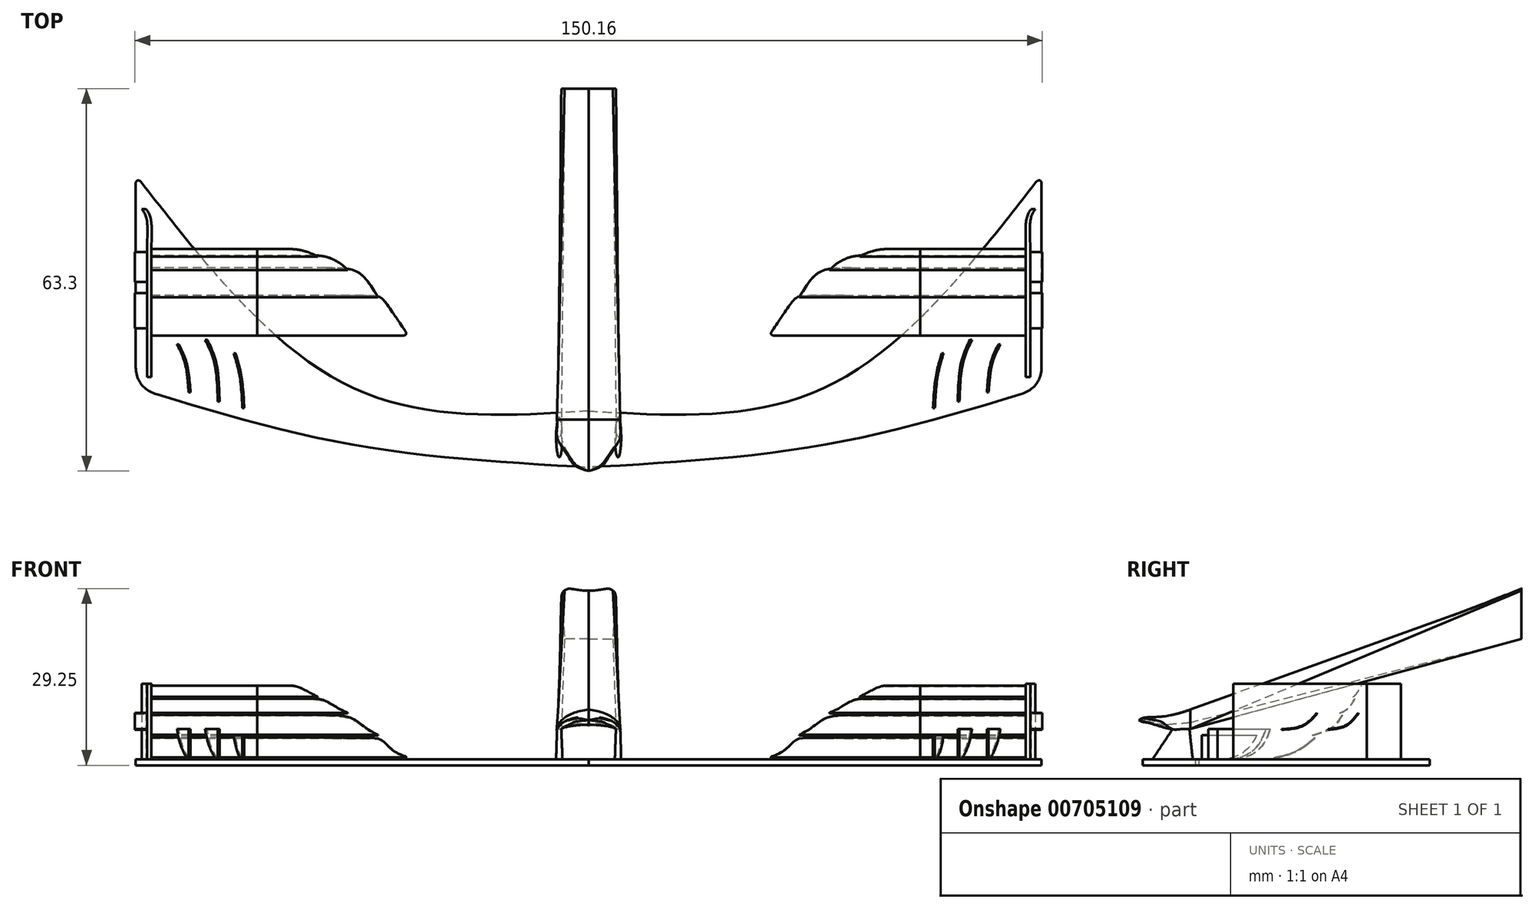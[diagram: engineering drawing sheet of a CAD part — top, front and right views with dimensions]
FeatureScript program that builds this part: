
annotation { "Feature Type Name" : "Feature", "Feature Type Description" : "" }
export const myFeature = defineFeature(function(context is Context, id is Id, definition is map)
    precondition{}
    {
        {
            var Q0;
            Q0=qCreatedBy(makeId("Top.planeOp"),FACE);
            var sketch = newSketch(context, id + "F0", { "sketchPlane" : qUnion([Q0])});
            skLineSegment(sketch, "E0", {"start": v(74.97, -59.54) * mm, "end": v(74.97, -24.29) * mm});
            skFitSpline(sketch, "E1", {"points": [v(74.97, -59.54) * mm, v(39.02, -68.96) * mm, v(0, -72.68) * mm], "startDerivative": vector(-71.84, -22) * mm, "endDerivative": vector(-78.07, -4.37) * mm});
            skFitSpline(sketch, "E2", {"points": [v(0, -63.37) * mm, v(39.02, -59.54) * mm, v(74.97, -24.29) * mm], "startDerivative": vector(86.9, -5.45) * mm, "endDerivative": vector(63.53, 81.8) * mm});
            skFitSpline(sketch, "E3.MirrorCS", {"points": [v(0, -63.37) * mm, v(-39.02, -59.54) * mm, v(-74.97, -24.29) * mm], "startDerivative": vector(-86.9, -5.45) * mm, "endDerivative": vector(-63.53, 81.8) * mm});
            skLineSegment(sketch, "E4.MirrorCS", {"start": v(-74.97, -59.54) * mm, "end": v(-74.97, -24.29) * mm});
            skFitSpline(sketch, "E5.MirrorCS", {"points": [v(-74.97, -59.54) * mm, v(-39.02, -68.96) * mm, v(0, -72.68) * mm], "startDerivative": vector(71.84, -22) * mm, "endDerivative": vector(78.07, -4.37) * mm});
            skSolve(sketch);
        }
        {
            var Q0;
            Q0 = qSketchRegion(id + "F0", true);
            extrude(context, id + "F1", {"entities" : qUnion([Q0]), "depth" : 1 * mm, "offsetDistance" : 25 * mm});
        }
        {
            var Q0;
            Q0=makeQuery(id+"F1.opExtrude","CAP_FACE",FACE,{"disambiguationData":[OSD([sQuery(id+"F0.wireOp",EDGE,"E0"),sQuery(id+"F0.wireOp",EDGE,"E1"),sQuery(id+"F0.wireOp",EDGE,"E2"),sQuery(id+"F0.wireOp",EDGE,"E3.MirrorCS"),sQuery(id+"F0.wireOp",EDGE,"E4.MirrorCS"),sQuery(id+"F0.wireOp",EDGE,"E5.MirrorCS")])],"isStart":false});
            var sketch = newSketch(context, id + "F2", { "sketchPlane" : qUnion([Q0])});
            skFitSpline(sketch, "E6", {"points": [v(65.9, -60.3) * mm, v(66.55, -55.36) * mm, v(67.83, -52.34) * mm], "startDerivative": vector(0.7, 9.56) * mm, "endDerivative": vector(3.24, 6.26) * mm});
            skFitSpline(sketch, "E7", {"points": [v(61.08, -61.82) * mm, v(61.66, -55.3) * mm, v(63.12, -51.58) * mm], "startDerivative": vector(0.4, 12.48) * mm, "endDerivative": vector(3.81, 7.8) * mm});
            skFitSpline(sketch, "E8", {"points": [v(57, -62.92) * mm, v(57.47, -57.63) * mm, v(58.46, -53.8) * mm], "startDerivative": vector(0.53, 10.29) * mm, "endDerivative": vector(2.43, 7.92) * mm});
            skFitSpline(sketch, "E9", {"points": [v(57.3, -62.92) * mm, v(57.76, -57.63) * mm, v(58.75, -53.8) * mm], "startDerivative": vector(0.53, 10.29) * mm, "endDerivative": vector(2.43, 7.92) * mm});
            skFitSpline(sketch, "E10", {"points": [v(61.37, -61.82) * mm, v(61.98, -55.3) * mm, v(63.46, -51.58) * mm], "startDerivative": vector(0.45, 12.5) * mm, "endDerivative": vector(3.88, 7.8) * mm});
            skFitSpline(sketch, "E11", {"points": [v(66.2, -60.3) * mm, v(66.84, -55.36) * mm, v(68.15, -52.34) * mm], "startDerivative": vector(0.68, 9.58) * mm, "endDerivative": vector(3.31, 6.25) * mm});
            skLineSegment(sketch, "E12", {"start": v(58.46, -53.8) * mm, "end": v(58.75, -53.8) * mm});
            skLineSegment(sketch, "E13", {"start": v(57.3, -62.92) * mm, "end": v(57, -62.92) * mm});
            skLineSegment(sketch, "E14", {"start": v(61.08, -61.82) * mm, "end": v(61.37, -61.82) * mm});
            skLineSegment(sketch, "E15", {"start": v(63.12, -51.58) * mm, "end": v(63.46, -51.58) * mm});
            skLineSegment(sketch, "E16", {"start": v(65.9, -60.3) * mm, "end": v(66.2, -60.3) * mm});
            skLineSegment(sketch, "E17", {"start": v(67.83, -52.34) * mm, "end": v(68.15, -52.34) * mm});
            skFitSpline(sketch, "E18.MirrorCS", {"points": [v(-57, -62.92) * mm, v(-57.47, -57.63) * mm, v(-58.46, -53.8) * mm], "startDerivative": vector(-0.53, 10.29) * mm, "endDerivative": vector(-2.43, 7.92) * mm});
            skFitSpline(sketch, "E19.MirrorCS", {"points": [v(-57.3, -62.92) * mm, v(-57.76, -57.63) * mm, v(-58.75, -53.8) * mm], "startDerivative": vector(-0.53, 10.29) * mm, "endDerivative": vector(-2.43, 7.92) * mm});
            skLineSegment(sketch, "E20.MirrorCS", {"start": v(-57.3, -62.92) * mm, "end": v(-57, -62.92) * mm});
            skLineSegment(sketch, "E21.MirrorCS", {"start": v(-58.46, -53.8) * mm, "end": v(-58.75, -53.8) * mm});
            skLineSegment(sketch, "E22.MirrorCS", {"start": v(-61.08, -61.82) * mm, "end": v(-61.37, -61.82) * mm});
            skLineSegment(sketch, "E23.MirrorCS", {"start": v(-65.9, -60.3) * mm, "end": v(-66.2, -60.3) * mm});
            skFitSpline(sketch, "E24.MirrorCS", {"points": [v(-65.9, -60.3) * mm, v(-66.55, -55.36) * mm, v(-67.83, -52.34) * mm], "startDerivative": vector(-0.7, 9.56) * mm, "endDerivative": vector(-3.24, 6.26) * mm});
            skFitSpline(sketch, "E25.MirrorCS", {"points": [v(-66.2, -60.3) * mm, v(-66.84, -55.36) * mm, v(-68.15, -52.34) * mm], "startDerivative": vector(-0.68, 9.58) * mm, "endDerivative": vector(-3.31, 6.25) * mm});
            skFitSpline(sketch, "E26.MirrorCS", {"points": [v(-61.37, -61.82) * mm, v(-61.98, -55.3) * mm, v(-63.46, -51.58) * mm], "startDerivative": vector(-0.45, 12.5) * mm, "endDerivative": vector(-3.88, 7.8) * mm});
            skFitSpline(sketch, "E27.MirrorCS", {"points": [v(-61.08, -61.82) * mm, v(-61.66, -55.3) * mm, v(-63.12, -51.58) * mm], "startDerivative": vector(-0.4, 12.48) * mm, "endDerivative": vector(-3.81, 7.8) * mm});
            skLineSegment(sketch, "E28.MirrorCS", {"start": v(-63.12, -51.58) * mm, "end": v(-63.46, -51.58) * mm});
            skLineSegment(sketch, "E29.MirrorCS", {"start": v(-67.83, -52.34) * mm, "end": v(-68.15, -52.34) * mm});
            skLineSegment(sketch, "E30", {"start": v(73.08, -57.72) * mm, "end": v(73.08, -35.62) * mm});
            skLineSegment(sketch, "E31", {"start": v(73.08, -35.62) * mm, "end": v(72.35, -35.62) * mm});
            skLineSegment(sketch, "E32", {"start": v(72.35, -35.62) * mm, "end": v(72.35, -57.72) * mm});
            skLineSegment(sketch, "E33", {"start": v(72.35, -57.72) * mm, "end": v(73.08, -57.72) * mm});
            skFitSpline(sketch, "E34", {"points": [v(72.35, -35.62) * mm, v(72.52, -31.33) * mm, v(73.25, -29.91) * mm], "startDerivative": vector(-0.23, 7.88) * mm, "endDerivative": vector(2.23, 3.15) * mm});
            skFitSpline(sketch, "E35", {"points": [v(73.08, -35.62) * mm, v(73.21, -31.33) * mm, v(73.94, -29.91) * mm], "startDerivative": vector(-0.32, 7.88) * mm, "endDerivative": vector(2.24, 3.15) * mm});
            skLineSegment(sketch, "E36", {"start": v(73.25, -29.91) * mm, "end": v(73.94, -29.91) * mm});
            skLineSegment(sketch, "E37.MirrorCS", {"start": v(-73.08, -57.72) * mm, "end": v(-73.08, -35.62) * mm});
            skLineSegment(sketch, "E38.MirrorCS", {"start": v(-73.08, -35.62) * mm, "end": v(-72.35, -35.62) * mm});
            skLineSegment(sketch, "E39.MirrorCS", {"start": v(-72.35, -35.62) * mm, "end": v(-72.35, -57.72) * mm});
            skFitSpline(sketch, "E40.MirrorCS", {"points": [v(-72.35, -35.62) * mm, v(-72.52, -31.33) * mm, v(-73.25, -29.91) * mm], "startDerivative": vector(0.23, 7.88) * mm, "endDerivative": vector(-2.23, 3.15) * mm});
            skFitSpline(sketch, "E41.MirrorCS", {"points": [v(-73.08, -35.62) * mm, v(-73.21, -31.33) * mm, v(-73.94, -29.91) * mm], "startDerivative": vector(0.32, 7.88) * mm, "endDerivative": vector(-2.24, 3.15) * mm});
            skLineSegment(sketch, "E42.MirrorCS", {"start": v(-73.25, -29.91) * mm, "end": v(-73.94, -29.91) * mm});
            skLineSegment(sketch, "E43.MirrorCS", {"start": v(-72.35, -57.72) * mm, "end": v(-73.08, -57.72) * mm});
            skSolve(sketch);
        }
        {
            var Q0;
            Q0=makeQuery(id+"F2.imprint","IMPRINT",FACE,{"disambiguationData":[TD([[makeQuery(id+"F2.imprint","IMPRINT",EDGE,{"derivedFrom":sQuery(id+"F2.wireOp",EDGE,"E30")}),1.0]])]});
            var Q1;
            Q1=makeQuery(id+"F2.imprint","IMPRINT",FACE,{"disambiguationData":[TD([[makeQuery(id+"F2.imprint","IMPRINT",EDGE,{"derivedFrom":sQuery(id+"F2.wireOp",EDGE,"E31")}),-1.0]])]});
            var Q2;
            Q2=makeQuery(id+"F2.imprint","IMPRINT",FACE,{"disambiguationData":[TD([[makeQuery(id+"F2.imprint","IMPRINT",EDGE,{"derivedFrom":sQuery(id+"F2.wireOp",EDGE,"E37.MirrorCS")}),-1.0]])]});
            var Q3;
            Q3=makeQuery(id+"F2.imprint","IMPRINT",FACE,{"disambiguationData":[TD([[makeQuery(id+"F2.imprint","IMPRINT",EDGE,{"derivedFrom":sQuery(id+"F2.wireOp",EDGE,"E38.MirrorCS")}),1.0]])]});
            extrude(context, id + "F3", {"entities" : qUnion([Q0, Q1, Q2, Q3]), "depth" : 12.5 * mm, "offsetDistance" : 25 * mm});
        }
        {
            var Q0;
            Q0=makeQuery(id+"F2.imprint","IMPRINT",FACE,{"disambiguationData":[TD([[makeQuery(id+"F2.imprint","IMPRINT",EDGE,{"derivedFrom":sQuery(id+"F2.wireOp",EDGE,"E6")}),-1.0]])]});
            var Q1;
            Q1=makeQuery(id+"F2.imprint","IMPRINT",FACE,{"disambiguationData":[TD([[makeQuery(id+"F2.imprint","IMPRINT",EDGE,{"derivedFrom":sQuery(id+"F2.wireOp",EDGE,"E7")}),-1.0]])]});
            var Q2;
            Q2=makeQuery(id+"F2.imprint","IMPRINT",FACE,{"disambiguationData":[TD([[makeQuery(id+"F2.imprint","IMPRINT",EDGE,{"derivedFrom":sQuery(id+"F2.wireOp",EDGE,"E23.MirrorCS")}),-1.0]])]});
            var Q3;
            Q3=makeQuery(id+"F2.imprint","IMPRINT",FACE,{"disambiguationData":[TD([[makeQuery(id+"F2.imprint","IMPRINT",EDGE,{"derivedFrom":sQuery(id+"F2.wireOp",EDGE,"E22.MirrorCS")}),-1.0]])]});
            extrude(context, id + "F4", {"entities" : qUnion([Q0, Q1, Q2, Q3]), "depth" : 5 * mm, "offsetDistance" : 25 * mm});
        }
        {
            var Q0;
            Q0=makeQuery(id+"F2.imprint","IMPRINT",FACE,{"disambiguationData":[TD([[makeQuery(id+"F2.imprint","IMPRINT",EDGE,{"derivedFrom":sQuery(id+"F2.wireOp",EDGE,"E18.MirrorCS")}),1.0]])]});
            var Q1;
            Q1=makeQuery(id+"F2.imprint","IMPRINT",FACE,{"disambiguationData":[TD([[makeQuery(id+"F2.imprint","IMPRINT",EDGE,{"derivedFrom":sQuery(id+"F2.wireOp",EDGE,"E8")}),-1.0]])]});
            extrude(context, id + "F5", {"entities" : qUnion([Q0, Q1]), "depth" : 4 * mm, "offsetDistance" : 25 * mm});
        }
        {
            var Q0;
            Q0=makeQuery(id+"F3.opExtrude","SWEPT_FACE",FACE,{"disambiguationData":[OSD([sQuery(id+"F2.wireOp",EDGE,"E39.MirrorCS")])]});
            var sketch = newSketch(context, id + "F6", { "sketchPlane" : qUnion([Q0])});
            skFitSpline(sketch, "E44", {"points": [v(-50.88, 1.32) * mm, v(-47.28, 2.4) * mm, v(-44.22, 4.58) * mm], "startDerivative": vector(7.48, 1.6) * mm, "endDerivative": vector(5.84, 4.92) * mm});
            skFitSpline(sketch, "E45", {"points": [v(-44.54, 5.04) * mm, v(-41.08, 6.5) * mm, v(-39.66, 8.33) * mm], "startDerivative": vector(7, 2.16) * mm, "endDerivative": vector(2.59, 4.5) * mm});
            skFitSpline(sketch, "E46", {"points": [v(-40.06, 8.7) * mm, v(-38.67, 9.5) * mm, v(-37.62, 11.03) * mm], "startDerivative": vector(3.11, 1.31) * mm, "endDerivative": vector(1.79, 3.32) * mm});
            skFitSpline(sketch, "E47", {"points": [v(-37.83, 11.32) * mm, v(-37.16, 12.08) * mm, v(-36.57, 13.16) * mm], "startDerivative": vector(1.48, 1.48) * mm, "endDerivative": vector(1.03, 2.18) * mm});
            skFitSpline(sketch, "E48", {"points": [v(-50.88, 1.19) * mm, v(-47.28, 2.25) * mm, v(-44.22, 4.44) * mm], "startDerivative": vector(7.49, 1.55) * mm, "endDerivative": vector(5.83, 4.95) * mm});
            skFitSpline(sketch, "E49", {"points": [v(-44.54, 4.92) * mm, v(-41.08, 6.35) * mm, v(-39.66, 8.16) * mm], "startDerivative": vector(7, 2.11) * mm, "endDerivative": vector(2.6, 4.46) * mm});
            skFitSpline(sketch, "E50", {"points": [v(-40.06, 8.6) * mm, v(-38.67, 9.38) * mm, v(-37.62, 10.87) * mm], "startDerivative": vector(3.1, 1.28) * mm, "endDerivative": vector(1.8, 3.22) * mm});
            skFitSpline(sketch, "E51", {"points": [v(-37.83, 11.28) * mm, v(-37.16, 12.03) * mm, v(-36.57, 13.07) * mm], "startDerivative": vector(1.47, 1.46) * mm, "endDerivative": vector(1.04, 2.11) * mm});
            skLineSegment(sketch, "E52", {"start": v(-36.57, 13.16) * mm, "end": v(-36.57, 13.07) * mm});
            skLineSegment(sketch, "E53", {"start": v(-37.83, 11.32) * mm, "end": v(-37.83, 11.28) * mm});
            skLineSegment(sketch, "E54", {"start": v(-37.62, 11.03) * mm, "end": v(-37.62, 10.87) * mm});
            skLineSegment(sketch, "E55", {"start": v(-40.06, 8.7) * mm, "end": v(-40.06, 8.6) * mm});
            skLineSegment(sketch, "E56", {"start": v(-39.66, 8.33) * mm, "end": v(-39.66, 8.16) * mm});
            skLineSegment(sketch, "E57", {"start": v(-44.54, 5.04) * mm, "end": v(-44.54, 4.92) * mm});
            skLineSegment(sketch, "E58", {"start": v(-44.22, 4.58) * mm, "end": v(-44.22, 4.44) * mm});
            skLineSegment(sketch, "E59", {"start": v(-50.88, 1.32) * mm, "end": v(-50.88, 1.19) * mm});
            skSolve(sketch);
        }
        {
            var Q0;
            Q0 = qSketchRegion(id + "F6", true);
            extrude(context, id + "F7", {"entities" : qUnion([Q0]), "depth" : 17.5 * mm, "offsetDistance" : 25 * mm});
        }
        {
            var Q0;
            Q0=makeQuery(id+"F7.opExtrude","CAP_FACE",FACE,{"disambiguationData":[OSD([sQuery(id+"F6.wireOp",EDGE,"E44"),sQuery(id+"F6.wireOp",EDGE,"E48"),sQuery(id+"F6.wireOp",EDGE,"E58"),sQuery(id+"F6.wireOp",EDGE,"E59")])],"isStart":false});
            var sketch = newSketch(context, id + "F8", { "sketchPlane" : qUnion([Q0])});
            skLineSegment(sketch, "E60", {"start": v(-50.88, 1.19) * mm, "end": v(-50.88, 1.32) * mm});
            skFitSpline(sketch, "E61", {"points": [v(-50.88, 1.19) * mm, v(-47.28, 2.24) * mm, v(-44.22, 4.44) * mm], "startDerivative": vector(7.5, 1.63) * mm, "endDerivative": vector(5.86, 4.9) * mm});
            skLineSegment(sketch, "E62", {"start": v(-44.22, 4.44) * mm, "end": v(-44.22, 4.58) * mm});
            skFitSpline(sketch, "E63", {"points": [v(-44.22, 4.58) * mm, v(-47.28, 2.4) * mm, v(-50.88, 1.32) * mm], "startDerivative": vector(-5.84, -4.92) * mm, "endDerivative": vector(-7.48, -1.6) * mm});
            skLineSegment(sketch, "E64", {"start": v(-44.54, 4.92) * mm, "end": v(-44.54, 5.04) * mm});
            skLineSegment(sketch, "E65", {"start": v(-39.66, 8.16) * mm, "end": v(-39.66, 8.33) * mm});
            skLineSegment(sketch, "E66", {"start": v(-40.06, 8.61) * mm, "end": v(-40.06, 8.7) * mm});
            skFitSpline(sketch, "E67", {"points": [v(-39.66, 8.33) * mm, v(-41.08, 6.5) * mm, v(-44.54, 5.04) * mm], "startDerivative": vector(-2.6, -4.5) * mm, "endDerivative": vector(-7, -2.16) * mm});
            skFitSpline(sketch, "E68", {"points": [v(-44.54, 4.92) * mm, v(-41.08, 6.36) * mm, v(-39.66, 8.16) * mm], "startDerivative": vector(6.99, 2.14) * mm, "endDerivative": vector(2.6, 4.43) * mm});
            skFitSpline(sketch, "E69", {"points": [v(-40.06, 8.61) * mm, v(-38.67, 9.38) * mm, v(-37.62, 10.87) * mm], "startDerivative": vector(3.1, 1.28) * mm, "endDerivative": vector(1.8, 3.22) * mm});
            skLineSegment(sketch, "E70", {"start": v(-37.62, 10.87) * mm, "end": v(-37.62, 11.03) * mm});
            skFitSpline(sketch, "E71", {"points": [v(-40.06, 8.7) * mm, v(-38.67, 9.5) * mm, v(-37.62, 11.03) * mm], "startDerivative": vector(3.11, 1.3) * mm, "endDerivative": vector(1.79, 3.32) * mm});
            skLineSegment(sketch, "E72", {"start": v(-37.83, 11.28) * mm, "end": v(-37.83, 11.33) * mm});
            skLineSegment(sketch, "E73", {"start": v(-36.57, 13.07) * mm, "end": v(-36.57, 13.16) * mm});
            skFitSpline(sketch, "E74", {"points": [v(-36.57, 13.16) * mm, v(-37.16, 12.08) * mm, v(-37.83, 11.33) * mm], "startDerivative": vector(-1.03, -2.18) * mm, "endDerivative": vector(-1.48, -1.48) * mm});
            skFitSpline(sketch, "E75", {"points": [v(-37.83, 11.28) * mm, v(-37.16, 12.03) * mm, v(-36.57, 13.07) * mm], "startDerivative": vector(1.47, 1.46) * mm, "endDerivative": vector(1.04, 2.11) * mm});
            skSolve(sketch);
        }
        {
            var Q0;
            {var subQ10=sQuery(id+"F8.wireOp",EDGE,"E60");Q0=makeQuery(id+"F8.imprint","IMPRINT",FACE,{"disambiguationData":[TD([[makeQuery(id+"F8.imprint","IMPRINT",EDGE,{"derivedFrom":subQ10}),1.0]])]});}
            extrude(context, id + "F9", {"entities" : qUnion([Q0]), "depth" : 25 * mm, "offsetDistance" : 25 * mm});
        }
        {
            var Q0;
            Q0=makeQuery(id+"F7.opExtrude","CAP_FACE",FACE,{"disambiguationData":[OSD([sQuery(id+"F6.wireOp",EDGE,"E45"),sQuery(id+"F6.wireOp",EDGE,"E49"),sQuery(id+"F6.wireOp",EDGE,"E56"),sQuery(id+"F6.wireOp",EDGE,"E57")])],"isStart":false});
            extrude(context, id + "F10", {"entities" : qUnion([Q0]), "depth" : 20 * mm, "offsetDistance" : 25 * mm});
        }
        {
            var Q0;
            Q0=makeQuery(id+"F7.opExtrude","CAP_FACE",FACE,{"disambiguationData":[OSD([sQuery(id+"F6.wireOp",EDGE,"E46"),sQuery(id+"F6.wireOp",EDGE,"E50"),sQuery(id+"F6.wireOp",EDGE,"E54"),sQuery(id+"F6.wireOp",EDGE,"E55")])],"isStart":false});
            extrude(context, id + "F11", {"entities" : qUnion([Q0]), "depth" : 15 * mm, "offsetDistance" : 25 * mm});
        }
        {
            var Q0;
            Q0=makeQuery(id+"F7.opExtrude","CAP_FACE",FACE,{"disambiguationData":[OSD([sQuery(id+"F6.wireOp",EDGE,"E47"),sQuery(id+"F6.wireOp",EDGE,"E51"),sQuery(id+"F6.wireOp",EDGE,"E52"),sQuery(id+"F6.wireOp",EDGE,"E53")])],"isStart":false});
            extrude(context, id + "F12", {"entities" : qUnion([Q0]), "depth" : 10 * mm, "offsetDistance" : 25 * mm});
        }
        {
            var Q0;
            Q0=makeQuery(id+"F9.opExtrude","CAP_EDGE",EDGE,{"disambiguationData":[OSD([sQuery(id+"F8.wireOp",EDGE,"E62")])],"isStart":false});
            fillet(context, id + "F13", {"entities" : qUnion([Q0]), "radius" : 15 * mm, "tangentPropagation" : true, "rho" : 0.9, "crossSection" : FilletCrossSection.CONIC, "allowEdgeOverflow" : false});
        }
        {
            var Q0;
            Q0=makeQuery(id+"F10.opExtrude","CAP_EDGE",EDGE,{"disambiguationData":[OSD([sQuery(id+"F6.wireOp",EDGE,"E56")])],"isStart":false});
            fillet(context, id + "F14", {"entities" : qUnion([Q0]), "radius" : 10 * mm, "tangentPropagation" : true, "rho" : 0.7, "crossSection" : FilletCrossSection.CONIC, "allowEdgeOverflow" : false});
        }
        {
            var Q0;
            Q0=makeQuery(id+"F11.opExtrude","CAP_EDGE",EDGE,{"disambiguationData":[OSD([sQuery(id+"F6.wireOp",EDGE,"E54")])],"isStart":false});
            fillet(context, id + "F15", {"entities" : qUnion([Q0]), "radius" : 7.5 * mm, "tangentPropagation" : true, "rho" : 0.5, "crossSection" : FilletCrossSection.CONIC, "allowEdgeOverflow" : false});
        }
        {
            var Q0;
            Q0=makeQuery(id+"F12.opExtrude","CAP_EDGE",EDGE,{"disambiguationData":[OSD([sQuery(id+"F6.wireOp",EDGE,"E52")])],"isStart":false});
            fillet(context, id + "F16", {"entities" : qUnion([Q0]), "radius" : 7.5 * mm, "tangentPropagation" : true, "rho" : 0.4, "crossSection" : FilletCrossSection.CONIC, "allowEdgeOverflow" : false});
        }
        {
            var Q0;
            Q0=makeQuery(id+"F7.opExtrude","SWEPT_BODY",BODY,{"disambiguationData":[OSD([sQuery(id+"F6.wireOp",EDGE,"E47"),sQuery(id+"F6.wireOp",EDGE,"E51"),sQuery(id+"F6.wireOp",EDGE,"E52"),sQuery(id+"F6.wireOp",EDGE,"E53")])]});
            var Q1;
            Q1=makeQuery(id+"F7.opExtrude","SWEPT_BODY",BODY,{"disambiguationData":[OSD([sQuery(id+"F6.wireOp",EDGE,"E46"),sQuery(id+"F6.wireOp",EDGE,"E50"),sQuery(id+"F6.wireOp",EDGE,"E54"),sQuery(id+"F6.wireOp",EDGE,"E55")])]});
            var Q2;
            Q2=makeQuery(id+"F7.opExtrude","SWEPT_BODY",BODY,{"disambiguationData":[OSD([sQuery(id+"F6.wireOp",EDGE,"E45"),sQuery(id+"F6.wireOp",EDGE,"E49"),sQuery(id+"F6.wireOp",EDGE,"E56"),sQuery(id+"F6.wireOp",EDGE,"E57")])]});
            var Q3;
            Q3=makeQuery(id+"F7.opExtrude","SWEPT_BODY",BODY,{"disambiguationData":[OSD([sQuery(id+"F6.wireOp",EDGE,"E44"),sQuery(id+"F6.wireOp",EDGE,"E48"),sQuery(id+"F6.wireOp",EDGE,"E58"),sQuery(id+"F6.wireOp",EDGE,"E59")])]});
            var Q4;
            Q4=makeQuery(id+"F9.opExtrude","SWEPT_BODY",BODY,{"disambiguationData":[OSD([sQuery(id+"F6.wireOp",EDGE,"E44"),sQuery(id+"F8.wireOp",EDGE,"E60"),sQuery(id+"F8.wireOp",EDGE,"E61"),sQuery(id+"F8.wireOp",EDGE,"E62"),sQuery(id+"F8.wireOp",EDGE,"E63")])]});
            var Q5;
            Q5=makeQuery(id+"F10.opExtrude","SWEPT_BODY",BODY,{"disambiguationData":[OSD([sQuery(id+"F6.wireOp",EDGE,"E45"),sQuery(id+"F6.wireOp",EDGE,"E49"),sQuery(id+"F6.wireOp",EDGE,"E56"),sQuery(id+"F6.wireOp",EDGE,"E57")])]});
            var Q6;
            Q6=makeQuery(id+"F11.opExtrude","SWEPT_BODY",BODY,{"disambiguationData":[OSD([sQuery(id+"F6.wireOp",EDGE,"E46"),sQuery(id+"F6.wireOp",EDGE,"E50"),sQuery(id+"F6.wireOp",EDGE,"E54"),sQuery(id+"F6.wireOp",EDGE,"E55")])]});
            var Q7;
            Q7=makeQuery(id+"F12.opExtrude","SWEPT_BODY",BODY,{"disambiguationData":[OSD([sQuery(id+"F6.wireOp",EDGE,"E47"),sQuery(id+"F6.wireOp",EDGE,"E51"),sQuery(id+"F6.wireOp",EDGE,"E52"),sQuery(id+"F6.wireOp",EDGE,"E53")])]});
            var Q8;
            Q8=qCreatedBy(makeId("Right.planeOp"),FACE);
            mirror(context, id + "F17", {"entities" : qUnion([Q0, Q1, Q2, Q3, Q4, Q5, Q6, Q7]), "mirrorPlane" : qUnion([Q8])});
        }
        {
            var Q0;
            Q0=makeQuery(id+"F13.opFillet","BLEND_EDGE",EDGE,{"blendedFrom":[makeQuery(id+"F9.opExtrude","CAP_EDGE",EDGE,{"disambiguationData":[OSD([sQuery(id+"F8.wireOp",EDGE,"E62")])],"isStart":false}),makeQuery(id+"F9.opExtrude","SWEPT_FACE",FACE,{"disambiguationData":[OSD([sQuery(id+"F8.wireOp",EDGE,"E60")])]})],"blendedInto":[makeQuery(id+"F9.opExtrude","SWEPT_FACE",FACE,{"disambiguationData":[OSD([sQuery(id+"F8.wireOp",EDGE,"E60")])]})]});
            fillet(context, id + "F18", {"entities" : qUnion([Q0]), "radius" : 0.5 * mm, "tangentPropagation" : true, "rho" : 0.5, "crossSection" : FilletCrossSection.CONIC, "allowEdgeOverflow" : false});
        }
        {
            var Q0;
            Q0=makeQuery(id+"F17.opPattern","COPY",EDGE,{"derivedFrom":makeQuery(id+"F13.opFillet","BLEND_EDGE",EDGE,{"blendedFrom":[makeQuery(id+"F9.opExtrude","CAP_EDGE",EDGE,{"disambiguationData":[OSD([sQuery(id+"F8.wireOp",EDGE,"E62")])],"isStart":false}),makeQuery(id+"F9.opExtrude","SWEPT_FACE",FACE,{"disambiguationData":[OSD([sQuery(id+"F8.wireOp",EDGE,"E60")])]})],"blendedInto":[makeQuery(id+"F9.opExtrude","SWEPT_FACE",FACE,{"disambiguationData":[OSD([sQuery(id+"F8.wireOp",EDGE,"E60")])]})]}),"instanceName":"1"});
            fillet(context, id + "F19", {"entities" : qUnion([Q0]), "radius" : 0.5 * mm, "tangentPropagation" : true, "rho" : 0.5, "crossSection" : FilletCrossSection.CONIC, "allowEdgeOverflow" : false});
        }
        {
            var Q0;
            Q0=makeQuery(id+"F1.opExtrude","SWEPT_EDGE",EDGE,{"disambiguationData":[OSD([sQuery(id+"F0.wireOp",EDGE,"E3.MirrorCS"),sQuery(id+"F0.wireOp",EDGE,"E4.MirrorCS")])]});
            var Q1;
            Q1=makeQuery(id+"F1.opExtrude","SWEPT_EDGE",EDGE,{"disambiguationData":[OSD([sQuery(id+"F0.wireOp",EDGE,"E0"),sQuery(id+"F0.wireOp",EDGE,"E2")])]});
            fillet(context, id + "F20", {"entities" : qUnion([Q0, Q1]), "radius" : 0.5 * mm, "tangentPropagation" : true, "rho" : 0.3, "crossSection" : FilletCrossSection.CONIC, "allowEdgeOverflow" : false});
        }
        {
            var Q0;
            Q0=makeQuery(id+"F1.opExtrude","SWEPT_EDGE",EDGE,{"disambiguationData":[OSD([sQuery(id+"F0.wireOp",EDGE,"E0"),sQuery(id+"F0.wireOp",EDGE,"E1")])]});
            var Q1;
            Q1=makeQuery(id+"F1.opExtrude","SWEPT_EDGE",EDGE,{"disambiguationData":[OSD([sQuery(id+"F0.wireOp",EDGE,"E4.MirrorCS"),sQuery(id+"F0.wireOp",EDGE,"E5.MirrorCS")])]});
            fillet(context, id + "F21", {"entities" : qUnion([Q0, Q1]), "radius" : 5 * mm, "tangentPropagation" : true, "rho" : 0.5, "crossSection" : FilletCrossSection.CONIC, "allowEdgeOverflow" : false});
        }
        {
            var Q0;
            Q0=makeQuery(id+"F5.opExtrude","CAP_EDGE",EDGE,{"disambiguationData":[OSD([sQuery(id+"F2.wireOp",EDGE,"E21.MirrorCS")])],"isStart":true});
            var Q1;
            Q1=makeQuery(id+"F4.opExtrude","CAP_EDGE",EDGE,{"disambiguationData":[OSD([sQuery(id+"F2.wireOp",EDGE,"E28.MirrorCS")])],"isStart":true});
            var Q2;
            Q2=makeQuery(id+"F4.opExtrude","CAP_EDGE",EDGE,{"disambiguationData":[OSD([sQuery(id+"F2.wireOp",EDGE,"E29.MirrorCS")])],"isStart":true});
            var Q3;
            Q3=makeQuery(id+"F5.opExtrude","CAP_EDGE",EDGE,{"disambiguationData":[OSD([sQuery(id+"F2.wireOp",EDGE,"E12")])],"isStart":true});
            var Q4;
            Q4=makeQuery(id+"F4.opExtrude","CAP_EDGE",EDGE,{"disambiguationData":[OSD([sQuery(id+"F2.wireOp",EDGE,"E15")])],"isStart":true});
            var Q5;
            Q5=makeQuery(id+"F4.opExtrude","CAP_EDGE",EDGE,{"disambiguationData":[OSD([sQuery(id+"F2.wireOp",EDGE,"E17")])],"isStart":true});
            fillet(context, id + "F22", {"entities" : qUnion([Q0, Q1, Q2, Q3, Q4, Q5]), "radius" : 6.8 * mm, "tangentPropagation" : true, "rho" : 0.5, "crossSection" : FilletCrossSection.CONIC, "allowEdgeOverflow" : false});
        }
        {
            var Q0;
            Q0=makeQuery(id+"F3.opExtrude","SWEPT_FACE",FACE,{"disambiguationData":[OSD([sQuery(id+"F2.wireOp",EDGE,"E37.MirrorCS")])]});
            var sketch = newSketch(context, id + "F23", { "sketchPlane" : qUnion([Q0])});
            skFitSpline(sketch, "E76", {"points": [v(42, 5.88) * mm, v(39.06, 6.5) * mm, v(37.02, 8.5) * mm], "startDerivative": vector(-6.23, 0.51) * mm, "endDerivative": vector(-3.72, 4.76) * mm});
            skFitSpline(sketch, "E77", {"points": [v(42, 6) * mm, v(39.06, 6.63) * mm, v(37.02, 8.67) * mm], "startDerivative": vector(-6.25, 0.5) * mm, "endDerivative": vector(-3.7, 4.85) * mm});
            skLineSegment(sketch, "E78", {"start": v(37.02, 8.5) * mm, "end": v(37.02, 8.67) * mm});
            skLineSegment(sketch, "E79", {"start": v(42, 5.88) * mm, "end": v(42, 6) * mm});
            skFitSpline(sketch, "E80", {"points": [v(49.7, 5.88) * mm, v(46.17, 6.5) * mm, v(43.85, 8.5) * mm], "startDerivative": vector(-7.3, 0.43) * mm, "endDerivative": vector(-4.36, 4.89) * mm});
            skFitSpline(sketch, "E81", {"points": [v(49.7, 6) * mm, v(46.17, 6.63) * mm, v(43.85, 8.67) * mm], "startDerivative": vector(-7.3, 0.4) * mm, "endDerivative": vector(-4.34, 4.97) * mm});
            skLineSegment(sketch, "E82", {"start": v(43.85, 8.5) * mm, "end": v(43.85, 8.67) * mm});
            skLineSegment(sketch, "E83", {"start": v(49.7, 5.88) * mm, "end": v(49.7, 6) * mm});
            skSolve(sketch);
        }
        {
            var Q0;
            Q0 = qSketchRegion(id + "F23", true);
            extrude(context, id + "F24", {"entities" : qUnion([Q0]), "depth" : 2 * mm, "offsetDistance" : 25 * mm});
        }
        {
            var Q0;
            Q0=makeQuery(id+"F24.opExtrude","SWEPT_BODY",BODY,{"disambiguationData":[OSD([sQuery(id+"F23.wireOp",EDGE,"E80"),sQuery(id+"F23.wireOp",EDGE,"E81"),sQuery(id+"F23.wireOp",EDGE,"E82"),sQuery(id+"F23.wireOp",EDGE,"E83")])]});
            var Q1;
            Q1=makeQuery(id+"F24.opExtrude","SWEPT_BODY",BODY,{"disambiguationData":[OSD([sQuery(id+"F23.wireOp",EDGE,"E76"),sQuery(id+"F23.wireOp",EDGE,"E77"),sQuery(id+"F23.wireOp",EDGE,"E78"),sQuery(id+"F23.wireOp",EDGE,"E79")])]});
            var Q2;
            Q2=qCreatedBy(makeId("Right.planeOp"),FACE);
            mirror(context, id + "F25", {"entities" : qUnion([Q0, Q1]), "mirrorPlane" : qUnion([Q2])});
        }
        {
            var Q0;
            Q0=makeQuery(id+"F1.opExtrude","CAP_FACE",FACE,{"disambiguationData":[OSD([sQuery(id+"F0.wireOp",EDGE,"E0"),sQuery(id+"F0.wireOp",EDGE,"E1"),sQuery(id+"F0.wireOp",EDGE,"E2"),sQuery(id+"F0.wireOp",EDGE,"E3.MirrorCS"),sQuery(id+"F0.wireOp",EDGE,"E4.MirrorCS"),sQuery(id+"F0.wireOp",EDGE,"E5.MirrorCS")])],"isStart":false});
            var sketch = newSketch(context, id + "F26", { "sketchPlane" : qUnion([Q0])});
            skEllipse(sketch, "E84", {"center": v(4.86, -67.72) * mm, "majorRadius": 3.32 * mm, "minorRadius": 0.52 * mm, "majorAxis": v(0, -1)});
            skSolve(sketch);
        }
        {
            var Q0;
            Q0=makeQuery(id+"F26.imprint","IMPRINT",FACE,{"disambiguationData":[TD([[makeQuery(id+"F26.imprint","IMPRINT",EDGE,{"derivedFrom":sQuery(id+"F26.wireOp",EDGE,"E84")}),-1.0]])]});
            cPlane(context, id + "F27", {"entities" : qUnion([Q0]), "cplaneType" : CPlaneType.OFFSET, "offset" : 5 * mm, "width" : 150 * mm, "height" : 150 * mm});
        }
        {
            var Q0;
            Q0=qCreatedBy(id+"F27.planeOp",FACE);
            var sketch = newSketch(context, id + "F28", { "sketchPlane" : qUnion([Q0])});
            skEllipse(sketch, "E85", {"center": v(4.88, -66.34) * mm, "majorRadius": 1.4 * mm, "minorRadius": 0.36 * mm, "majorAxis": v(0, -1)});
            skSolve(sketch);
        }
        {
            var Q1;
            Q1=makeQuery(id+"F26.imprint","IMPRINT",FACE,{"disambiguationData":[TD([[makeQuery(id+"F26.imprint","IMPRINT",EDGE,{"derivedFrom":sQuery(id+"F26.wireOp",EDGE,"E84")}),1.0]])]});
            var Q2;
            Q2=makeQuery(id+"F28.imprint","IMPRINT",FACE,{"disambiguationData":[TD([[makeQuery(id+"F28.imprint","IMPRINT",EDGE,{"derivedFrom":sQuery(id+"F28.wireOp",EDGE,"E85")}),1.0]])]});
            loft(context, id + "F29", {"sheetProfilesArray" : [{ "sheetProfileEntities" : qUnion([Q1]) }, { "sheetProfileEntities" : qUnion([Q2]) }]});
        }
        {
            var Q0;
            Q0=makeQuery(id+"F29.opLoft","SWEPT_BODY",BODY,{"disambiguationData":[OSD([makeQuery(id+"F26.imprint","IMPRINT",FACE,{"disambiguationData":[TD([[makeQuery(id+"F26.imprint","IMPRINT",EDGE,{"derivedFrom":sQuery(id+"F26.wireOp",EDGE,"E84")}),1.0]])]}),makeQuery(id+"F28.imprint","IMPRINT",FACE,{"disambiguationData":[TD([[makeQuery(id+"F28.imprint","IMPRINT",EDGE,{"derivedFrom":sQuery(id+"F28.wireOp",EDGE,"E85")}),1.0]])]})])]});
            var Q1;
            Q1=qCreatedBy(makeId("Right.planeOp"),FACE);
            mirror(context, id + "F30", {"entities" : qUnion([Q0]), "mirrorPlane" : qUnion([Q1])});
        }
        {
            var Q0;
            Q0=qCreatedBy(makeId("Front.planeOp"),FACE);
            cPlane(context, id + "F31", {"entities" : qUnion([Q0]), "cplaneType" : CPlaneType.OFFSET, "offset" : 64.8 * mm, "width" : 150 * mm, "height" : 150 * mm});
        }
        {
            var Q0;
            Q0=qCreatedBy(id+"F31.planeOp",FACE);
            var sketch = newSketch(context, id + "F32", { "sketchPlane" : qUnion([Q0])});
            skPoint(sketch, "E86", {"position": v(-5.24, 6) * mm});
            skPoint(sketch, "E87", {"position": v(-4.52, 6) * mm});
            skPoint(sketch, "E88", {"position": v(4.51, 6) * mm});
            skPoint(sketch, "E89", {"position": v(5.24, 6) * mm});
            skFitSpline(sketch, "E90", {"points": [v(-4.52, 6) * mm, v(-4.2, 6.5) * mm, v(0, 7.05) * mm], "startDerivative": vector(0.53, 2.01) * mm, "endDerivative": vector(7.46, 0.33) * mm});
            skLineSegment(sketch, "E91", {"start": v(-4.52, 6) * mm, "end": v(-5.24, 6) * mm});
            skFitSpline(sketch, "E92", {"points": [v(-5.24, 6) * mm, v(-4.57, 7.39) * mm, v(0, 9.22) * mm], "startDerivative": vector(0.34, 3.13) * mm, "endDerivative": vector(9.01, 0.8) * mm});
            skLineSegment(sketch, "E93", {"start": v(0, 9.22) * mm, "end": v(0, 7.05) * mm});
            skFitSpline(sketch, "E94.MirrorCS", {"points": [v(5.24, 6) * mm, v(4.57, 7.39) * mm, v(0, 9.22) * mm], "startDerivative": vector(-0.34, 3.13) * mm, "endDerivative": vector(-9.01, 0.8) * mm});
            skFitSpline(sketch, "E95.MirrorCS", {"points": [v(4.52, 6) * mm, v(4.2, 6.5) * mm, v(0, 7.05) * mm], "startDerivative": vector(-0.53, 2.01) * mm, "endDerivative": vector(-7.46, 0.33) * mm});
            skLineSegment(sketch, "E96.MirrorCS", {"start": v(4.52, 6) * mm, "end": v(5.24, 6) * mm});
            skSolve(sketch);
        }
        {
            var Q0;
            Q0=qCreatedBy(id+"F31.planeOp",FACE);
            cPlane(context, id + "F33", {"entities" : qUnion([Q0]), "cplaneType" : CPlaneType.OFFSET, "offset" : 1.5 * mm, "width" : 150 * mm, "height" : 150 * mm});
        }
        {
            var Q0;
            Q0=qCreatedBy(id+"F33.planeOp",FACE);
            var sketch = newSketch(context, id + "F34", { "sketchPlane" : qUnion([Q0])});
            skPoint(sketch, "E97", {"position": v(-5.24, 6) * mm});
            skPoint(sketch, "E98", {"position": v(-4.52, 6) * mm});
            skPoint(sketch, "E99", {"position": v(4.51, 6) * mm});
            skPoint(sketch, "E100", {"position": v(5.24, 6) * mm});
            skLineSegment(sketch, "E101", {"start": v(-5.24, 6) * mm, "end": v(-4.52, 6) * mm});
            skLineSegment(sketch, "E102", {"start": v(4.51, 6) * mm, "end": v(5.24, 6) * mm});
            skFitSpline(sketch, "E103", {"points": [v(-4.52, 6) * mm, v(-4.16, 6.47) * mm, v(0, 6.9) * mm], "startDerivative": vector(0.72, 1.86) * mm, "endDerivative": vector(7.31, 0.18) * mm});
            skFitSpline(sketch, "E104", {"points": [v(-5.24, 6) * mm, v(-4.52, 7.27) * mm, v(0, 8.73) * mm], "startDerivative": vector(1.12, 3.8) * mm, "endDerivative": vector(7.3, 0.17) * mm});
            skLineSegment(sketch, "E105", {"start": v(0, 8.73) * mm, "end": v(0, 6.9) * mm});
            skFitSpline(sketch, "E106.MirrorCS", {"points": [v(4.52, 6) * mm, v(4.16, 6.47) * mm, v(0, 6.9) * mm], "startDerivative": vector(-0.72, 1.86) * mm, "endDerivative": vector(-7.31, 0.18) * mm});
            skFitSpline(sketch, "E107.MirrorCS", {"points": [v(5.24, 6) * mm, v(4.52, 7.27) * mm, v(0, 8.73) * mm], "startDerivative": vector(-1.12, 3.8) * mm, "endDerivative": vector(-7.3, 0.17) * mm});
            skLineSegment(sketch, "E108.MirrorCS", {"start": v(5.24, 6) * mm, "end": v(4.52, 6) * mm});
            skSolve(sketch);
        }
        {
            var Q0;
            Q0=qCreatedBy(id+"F33.planeOp",FACE);
            cPlane(context, id + "F35", {"entities" : qUnion([Q0]), "cplaneType" : CPlaneType.OFFSET, "offset" : 1.5 * mm, "width" : 150 * mm, "height" : 150 * mm});
        }
        {
            var Q0;
            Q0=qCreatedBy(id+"F35.planeOp",FACE);
            var sketch = newSketch(context, id + "F36", { "sketchPlane" : qUnion([Q0])});
            skPoint(sketch, "E109", {"position": v(-5.24, 6) * mm});
            skPoint(sketch, "E110", {"position": v(-4.52, 6) * mm});
            skPoint(sketch, "E111", {"position": v(4.52, 6) * mm});
            skPoint(sketch, "E112", {"position": v(5.24, 6) * mm});
            skLineSegment(sketch, "E113", {"start": v(4.52, 6) * mm, "end": v(5.24, 6) * mm});
            skLineSegment(sketch, "E114", {"start": v(-5.24, 6) * mm, "end": v(-4.52, 6) * mm});
            skFitSpline(sketch, "E115", {"points": [v(-4.52, 6) * mm, v(-4.12, 6.38) * mm, v(0, 6.8) * mm], "startDerivative": vector(0.93, 1.53) * mm, "endDerivative": vector(7.13, 0.25) * mm});
            skFitSpline(sketch, "E116", {"points": [v(-5.24, 6) * mm, v(-4.43, 7.14) * mm, v(0, 8.34) * mm], "startDerivative": vector(1.46, 3.44) * mm, "endDerivative": vector(7.28, 0.11) * mm});
            skLineSegment(sketch, "E117", {"start": v(0, 8.34) * mm, "end": v(0, 6.8) * mm});
            skFitSpline(sketch, "E118.MirrorCS", {"points": [v(4.52, 6) * mm, v(4.12, 6.38) * mm, v(0, 6.8) * mm], "startDerivative": vector(-0.93, 1.53) * mm, "endDerivative": vector(-7.13, 0.25) * mm});
            skFitSpline(sketch, "E119.MirrorCS", {"points": [v(5.24, 6) * mm, v(4.43, 7.14) * mm, v(0, 8.34) * mm], "startDerivative": vector(-1.46, 3.44) * mm, "endDerivative": vector(-7.28, 0.11) * mm});
            skLineSegment(sketch, "E120.MirrorCS", {"start": v(5.24, 6) * mm, "end": v(4.52, 6) * mm});
            skSolve(sketch);
        }
        {
            var Q0;
            Q0=qCreatedBy(id+"F35.planeOp",FACE);
            cPlane(context, id + "F37", {"entities" : qUnion([Q0]), "cplaneType" : CPlaneType.OFFSET, "offset" : 1.5 * mm, "width" : 150 * mm, "height" : 150 * mm});
        }
        {
            var Q0;
            Q0=qCreatedBy(id+"F37.planeOp",FACE);
            var sketch = newSketch(context, id + "F38", { "sketchPlane" : qUnion([Q0])});
            skLineSegment(sketch, "E121", {"start": v(0, 8.05) * mm, "end": v(0, 6.67) * mm});
            skFitSpline(sketch, "E122", {"points": [v(0, 6.67) * mm, v(-4.02, 6.3) * mm], "startDerivative": vector(-2.73, 0.39) * mm, "endDerivative": vector(-4.07, -0.96) * mm});
            skFitSpline(sketch, "E123", {"points": [v(0, 8.05) * mm, v(-4.33, 7.03) * mm], "startDerivative": vector(-2.8, 0.6) * mm, "endDerivative": vector(-4.15, -2.26) * mm});
            skFitSpline(sketch, "E124", {"points": [v(-4.33, 7.03) * mm, v(-4.02, 6.3) * mm], "startDerivative": vector(-0.83, -1.12) * mm, "endDerivative": vector(0.96, 0.08) * mm});
            skFitSpline(sketch, "E125.MirrorCS", {"points": [v(0, 6.67) * mm, v(4.02, 6.3) * mm], "startDerivative": vector(2.73, 0.39) * mm, "endDerivative": vector(4.07, -0.96) * mm});
            skFitSpline(sketch, "E126.MirrorCS", {"points": [v(0, 8.05) * mm, v(4.33, 7.03) * mm], "startDerivative": vector(2.8, 0.6) * mm, "endDerivative": vector(4.15, -2.26) * mm});
            skFitSpline(sketch, "E127.MirrorCS", {"points": [v(4.33, 7.03) * mm, v(4.02, 6.3) * mm], "startDerivative": vector(0.83, -1.12) * mm, "endDerivative": vector(-0.96, 0.08) * mm});
            skSolve(sketch);
        }
        {
            var Q0;
            Q0=qCreatedBy(id+"F37.planeOp",FACE);
            cPlane(context, id + "F39", {"entities" : qUnion([Q0]), "cplaneType" : CPlaneType.OFFSET, "offset" : 2 * mm, "width" : 150 * mm, "height" : 150 * mm});
        }
        {
            var Q0;
            Q0=qCreatedBy(id+"F39.planeOp",FACE);
            var sketch = newSketch(context, id + "F40", { "sketchPlane" : qUnion([Q0])});
            skLineSegment(sketch, "E128", {"start": v(0, 7.74) * mm, "end": v(0, 7.05) * mm});
            skFitSpline(sketch, "E129", {"points": [v(0, 7.05) * mm, v(-2.88, 6.92) * mm], "startDerivative": vector(-3.19, 0.68) * mm, "endDerivative": vector(-3.73, -0.61) * mm});
            skFitSpline(sketch, "E130", {"points": [v(0, 7.74) * mm, v(-2.9, 7.57) * mm], "startDerivative": vector(-1.27, 0.85) * mm, "endDerivative": vector(-3.12, -1.64) * mm});
            skFitSpline(sketch, "E131", {"points": [v(-2.9, 7.57) * mm, v(-2.88, 6.92) * mm], "startDerivative": vector(-1.1, -0.83) * mm, "endDerivative": vector(0.76, 0.04) * mm});
            skFitSpline(sketch, "E132.MirrorCS", {"points": [v(0, 7.05) * mm, v(2.88, 6.92) * mm], "startDerivative": vector(3.19, 0.68) * mm, "endDerivative": vector(3.73, -0.61) * mm});
            skFitSpline(sketch, "E133.MirrorCS", {"points": [v(0, 7.74) * mm, v(2.9, 7.57) * mm], "startDerivative": vector(1.27, 0.85) * mm, "endDerivative": vector(3.12, -1.64) * mm});
            skFitSpline(sketch, "E134.MirrorCS", {"points": [v(2.9, 7.57) * mm, v(2.88, 6.92) * mm], "startDerivative": vector(1.1, -0.83) * mm, "endDerivative": vector(-0.76, 0.04) * mm});
            skSolve(sketch);
        }
        {
            var Q0;
            Q0=qCreatedBy(id+"F39.planeOp",FACE);
            cPlane(context, id + "F41", {"entities" : qUnion([Q0]), "cplaneType" : CPlaneType.OFFSET, "offset" : 1.5 * mm, "width" : 150 * mm, "height" : 150 * mm});
        }
        {
            var Q0;
            Q0=qCreatedBy(id+"F41.planeOp",FACE);
            var sketch = newSketch(context, id + "F42", { "sketchPlane" : qUnion([Q0])});
            skLineSegment(sketch, "E135", {"start": v(0, 7.21) * mm, "end": v(0, 7.63) * mm});
            skFitSpline(sketch, "E136", {"points": [v(0, 7.63) * mm, v(1.36, 7.73) * mm], "startDerivative": vector(1.82, 0.63) * mm, "endDerivative": vector(0.68, -0.2) * mm});
            skFitSpline(sketch, "E137", {"points": [v(0, 7.21) * mm, v(1.48, 7.34) * mm], "startDerivative": vector(1.5, 0.46) * mm, "endDerivative": vector(0.65, 0.17) * mm});
            skFitSpline(sketch, "E138", {"points": [v(1.36, 7.73) * mm, v(1.48, 7.34) * mm], "startDerivative": vector(0.86, -0.25) * mm, "endDerivative": vector(-0.63, -0.14) * mm});
            skFitSpline(sketch, "E139.MirrorCS", {"points": [v(0, 7.63) * mm, v(-1.36, 7.73) * mm], "startDerivative": vector(-1.82, 0.63) * mm, "endDerivative": vector(-0.68, -0.2) * mm});
            skFitSpline(sketch, "E140.MirrorCS", {"points": [v(-1.36, 7.73) * mm, v(-1.48, 7.34) * mm], "startDerivative": vector(-0.86, -0.25) * mm, "endDerivative": vector(0.63, -0.14) * mm});
            skFitSpline(sketch, "E141.MirrorCS", {"points": [v(0, 7.21) * mm, v(-1.48, 7.34) * mm], "startDerivative": vector(-1.5, 0.46) * mm, "endDerivative": vector(-0.65, 0.17) * mm});
            skSolve(sketch);
        }
        {
            var Q0;
            Q0=qCreatedBy(id+"F41.planeOp",FACE);
            cPlane(context, id + "F43", {"entities" : qUnion([Q0]), "cplaneType" : CPlaneType.OFFSET, "offset" : 0.5 * mm, "width" : 150 * mm, "height" : 150 * mm});
        }
        {
            var Q0;
            Q0=qCreatedBy(id+"F43.planeOp",FACE);
            var sketch = newSketch(context, id + "F44", { "sketchPlane" : qUnion([Q0])});
            skPoint(sketch, "E142", {"position": v(0, 7.46) * mm});
            skSolve(sketch);
        }
        {
            var Q0;
            Q0=makeQuery(id+"F32.imprint","IMPRINT",FACE,{"disambiguationData":[TD([[makeQuery(id+"F32.imprint","IMPRINT",EDGE,{"derivedFrom":sQuery(id+"F32.wireOp",EDGE,"E93")}),1.0]])]});
            var Q1;
            Q1=makeQuery(id+"F34.imprint","IMPRINT",FACE,{"disambiguationData":[TD([[makeQuery(id+"F34.imprint","IMPRINT",EDGE,{"derivedFrom":sQuery(id+"F34.wireOp",EDGE,"E105")}),1.0]])]});
            var Q2;
            Q2=makeQuery(id+"F36.imprint","IMPRINT",FACE,{"disambiguationData":[TD([[makeQuery(id+"F36.imprint","IMPRINT",EDGE,{"derivedFrom":sQuery(id+"F36.wireOp",EDGE,"E117")}),1.0]])]});
            var Q3;
            Q3=makeQuery(id+"F38.imprint","IMPRINT",FACE,{"disambiguationData":[TD([[makeQuery(id+"F38.imprint","IMPRINT",EDGE,{"derivedFrom":sQuery(id+"F38.wireOp",EDGE,"E121")}),1.0]])]});
            var Q4;
            Q4=makeQuery(id+"F40.imprint","IMPRINT",FACE,{"disambiguationData":[TD([[makeQuery(id+"F40.imprint","IMPRINT",EDGE,{"derivedFrom":sQuery(id+"F40.wireOp",EDGE,"E128")}),1.0]])]});
            var Q5;
            Q5=makeQuery(id+"F42.imprint","IMPRINT",FACE,{"disambiguationData":[TD([[makeQuery(id+"F42.imprint","IMPRINT",EDGE,{"derivedFrom":sQuery(id+"F42.wireOp",EDGE,"E135")}),-1.0]])]});
            var Q6;
            Q6=sQuery(id+"F44.wireOp",VERTEX,"E142");
            loft(context, id + "F45", {"sheetProfilesArray" : [{ "sheetProfileEntities" : qUnion([Q0]) }, { "sheetProfileEntities" : qUnion([Q1]) }, { "sheetProfileEntities" : qUnion([Q2]) }, { "sheetProfileEntities" : qUnion([Q3]) }, { "sheetProfileEntities" : qUnion([Q4]) }, { "sheetProfileEntities" : qUnion([Q5]) }, { "sheetProfileEntities" : qUnion([Q6]) }]});
        }
        {
            var Q1;
            Q1=makeQuery(id+"F32.imprint","IMPRINT",FACE,{"disambiguationData":[TD([[makeQuery(id+"F32.imprint","IMPRINT",EDGE,{"derivedFrom":sQuery(id+"F32.wireOp",EDGE,"E90")}),1.0]])]});
            var Q2;
            Q2=makeQuery(id+"F34.imprint","IMPRINT",FACE,{"disambiguationData":[TD([[makeQuery(id+"F34.imprint","IMPRINT",EDGE,{"derivedFrom":sQuery(id+"F34.wireOp",EDGE,"E101")}),1.0]])]});
            var Q3;
            Q3=makeQuery(id+"F36.imprint","IMPRINT",FACE,{"disambiguationData":[TD([[makeQuery(id+"F36.imprint","IMPRINT",EDGE,{"derivedFrom":sQuery(id+"F36.wireOp",EDGE,"E114")}),1.0]])]});
            var Q4;
            Q4=makeQuery(id+"F38.imprint","IMPRINT",FACE,{"disambiguationData":[TD([[makeQuery(id+"F38.imprint","IMPRINT",EDGE,{"derivedFrom":sQuery(id+"F38.wireOp",EDGE,"E121")}),-1.0]])]});
            var Q5;
            Q5=makeQuery(id+"F40.imprint","IMPRINT",FACE,{"disambiguationData":[TD([[makeQuery(id+"F40.imprint","IMPRINT",EDGE,{"derivedFrom":sQuery(id+"F40.wireOp",EDGE,"E128")}),-1.0]])]});
            var Q6;
            Q6=makeQuery(id+"F42.imprint","IMPRINT",FACE,{"disambiguationData":[TD([[makeQuery(id+"F42.imprint","IMPRINT",EDGE,{"derivedFrom":sQuery(id+"F42.wireOp",EDGE,"E135")}),1.0]])]});
            var Q7;
            Q7=sQuery(id+"F44.wireOp",VERTEX,"E142");
            loft(context, id + "F46", {"sheetProfilesArray" : [{ "sheetProfileEntities" : qUnion([Q1]) }, { "sheetProfileEntities" : qUnion([Q2]) }, { "sheetProfileEntities" : qUnion([Q3]) }, { "sheetProfileEntities" : qUnion([Q4]) }, { "sheetProfileEntities" : qUnion([Q5]) }, { "sheetProfileEntities" : qUnion([Q6]) }, { "sheetProfileEntities" : qUnion([Q7]) }]});
        }
        {
            var Q0;
            Q0=qCreatedBy(id+"F31.planeOp",FACE);
            cPlane(context, id + "F47", {"entities" : qUnion([Q0]), "cplaneType" : CPlaneType.OFFSET, "offset" : 7.5 * mm, "oppositeDirection" : true, "width" : 150 * mm, "height" : 150 * mm});
        }
        {
            var Q0;
            Q0=qCreatedBy(makeId("Front.planeOp"),FACE);
            cPlane(context, id + "F48", {"entities" : qUnion([Q0]), "cplaneType" : CPlaneType.OFFSET, "offset" : 10 * mm, "width" : 150 * mm, "height" : 150 * mm});
        }
        {
            var Q0;
            Q0=qCreatedBy(id+"F48.planeOp",FACE);
            var sketch = newSketch(context, id + "F49", { "sketchPlane" : qUnion([Q0])});
            skLineSegment(sketch, "E143", {"start": v(0, 20.92) * mm, "end": v(0, 28.92) * mm});
            skFitSpline(sketch, "E144", {"points": [v(0, 28.92) * mm, v(4, 28.92) * mm], "startDerivative": vector(8, 0) * mm, "endDerivative": vector(2.44, -2.23) * mm});
            skFitSpline(sketch, "E145", {"points": [v(0, 20.92) * mm, v(4, 20.92) * mm], "startDerivative": vector(8, 0) * mm, "endDerivative": vector(8, 0) * mm});
            skFitSpline(sketch, "E146", {"points": [v(4, 28.92) * mm, v(4, 20.92) * mm], "startDerivative": vector(3.53, -1.04) * mm, "endDerivative": vector(0, -8) * mm});
            skFitSpline(sketch, "E147.MirrorCS", {"points": [v(0, 28.92) * mm, v(-4, 28.92) * mm], "startDerivative": vector(-8, 0) * mm, "endDerivative": vector(-2.44, -2.23) * mm});
            skFitSpline(sketch, "E148.MirrorCS", {"points": [v(-4, 28.92) * mm, v(-4, 20.92) * mm], "startDerivative": vector(-3.53, -1.04) * mm, "endDerivative": vector(0, -8) * mm});
            skFitSpline(sketch, "E149.MirrorCS", {"points": [v(0, 20.92) * mm, v(-4, 20.92) * mm], "startDerivative": vector(-8, 0) * mm, "endDerivative": vector(-8, 0) * mm});
            skSolve(sketch);
        }
        {
            var Q1;
            Q1=makeQuery(id+"F49.imprint","IMPRINT",FACE,{"disambiguationData":[TD([[makeQuery(id+"F49.imprint","IMPRINT",EDGE,{"derivedFrom":sQuery(id+"F49.wireOp",EDGE,"E143")}),-1.0]])]});
            var Q2;
            Q2=makeQuery(id+"F32.imprint","IMPRINT",FACE,{"disambiguationData":[TD([[makeQuery(id+"F32.imprint","IMPRINT",EDGE,{"derivedFrom":sQuery(id+"F32.wireOp",EDGE,"E93")}),1.0]])]});
            loft(context, id + "F50", {"sheetProfilesArray" : [{ "sheetProfileEntities" : qUnion([Q1]) }, { "sheetProfileEntities" : qUnion([Q2]) }]});
        }
        {
            var Q0;
            Q0=makeQuery(id+"F49.imprint","IMPRINT",FACE,{"disambiguationData":[TD([[makeQuery(id+"F49.imprint","IMPRINT",EDGE,{"derivedFrom":sQuery(id+"F49.wireOp",EDGE,"E143")}),1.0]])]});
            var Q1;
            Q1=makeQuery(id+"F32.imprint","IMPRINT",FACE,{"disambiguationData":[TD([[makeQuery(id+"F32.imprint","IMPRINT",EDGE,{"derivedFrom":sQuery(id+"F32.wireOp",EDGE,"E90")}),1.0]])]});
            loft(context, id + "F51", {"sheetProfilesArray" : [{ "sheetProfileEntities" : qUnion([Q0]) }, { "sheetProfileEntities" : qUnion([Q1]) }]});
        }
    });
